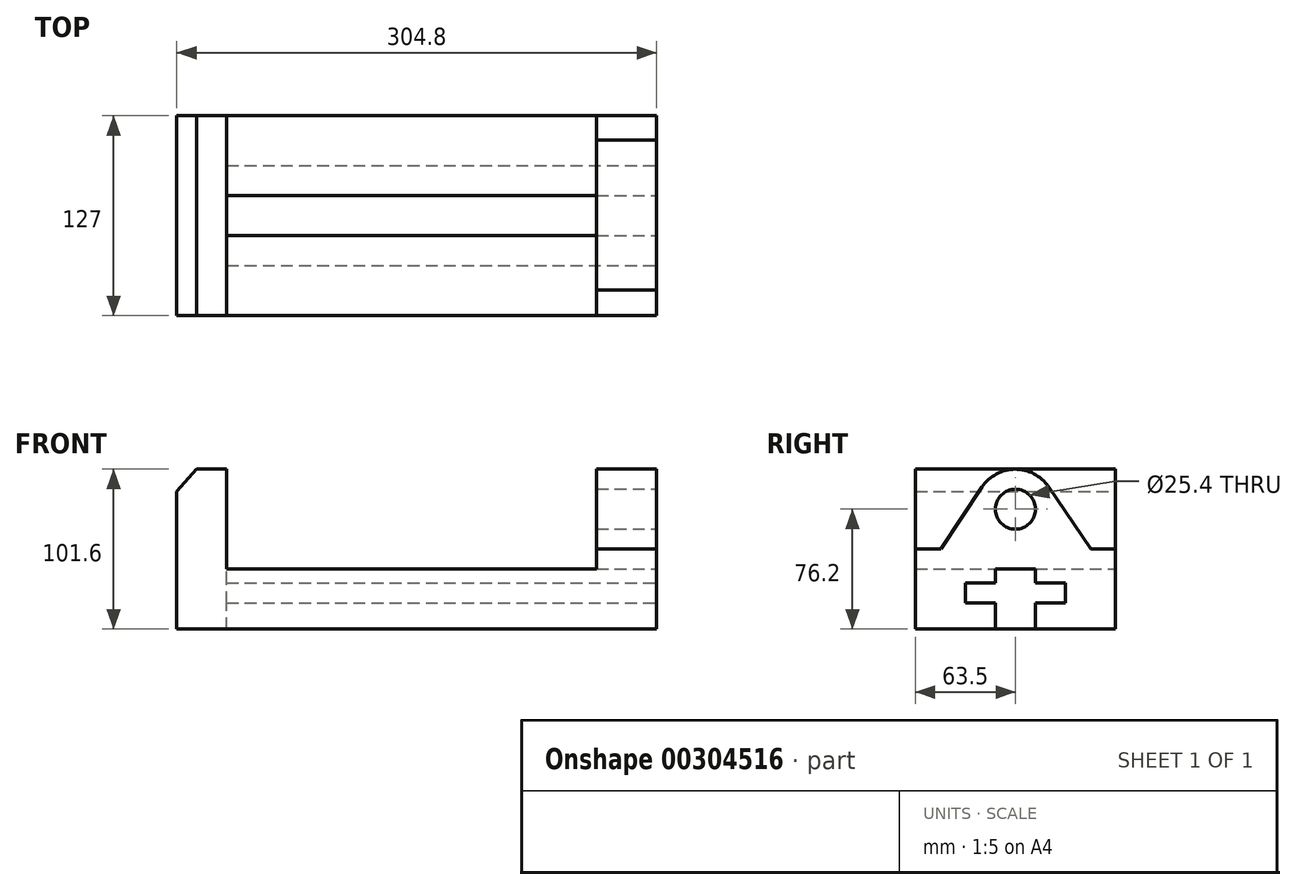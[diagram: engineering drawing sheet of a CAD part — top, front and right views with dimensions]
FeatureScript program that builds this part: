
annotation { "Feature Type Name" : "Feature", "Feature Type Description" : "" }
export const myFeature = defineFeature(function(context is Context, id is Id, definition is map)
    precondition{}
    {
        {
            var Q0;
            Q0=qCreatedBy(makeId("Front.planeOp"),FACE);
            var sketch = newSketch(context, id + "F0", { "sketchPlane" : qUnion([Q0])});
            skLineSegment(sketch, "E0", {"start": v(0, 0) * mm, "end": v(304.8, 0) * mm});
            skLineSegment(sketch, "E1", {"start": v(304.8, 0) * mm, "end": v(304.8, 101.6) * mm});
            skLineSegment(sketch, "E2", {"start": v(304.8, 101.6) * mm, "end": v(266.7, 101.6) * mm});
            skLineSegment(sketch, "E3", {"start": v(266.7, 101.6) * mm, "end": v(266.7, 38.1) * mm});
            skLineSegment(sketch, "E4", {"start": v(266.7, 38.1) * mm, "end": v(31.75, 38.1) * mm});
            skLineSegment(sketch, "E5", {"start": v(31.75, 38.1) * mm, "end": v(31.75, 101.6) * mm});
            skLineSegment(sketch, "E6", {"start": v(31.75, 101.6) * mm, "end": v(12.7, 101.6) * mm});
            skLineSegment(sketch, "E7", {"start": v(0, 87.4) * mm, "end": v(0, 0) * mm});
            skLineSegment(sketch, "E8", {"start": v(12.7, 101.6) * mm, "end": v(0, 87.4) * mm});
            skSolve(sketch);
        }
        {
            var Q0;
            Q0=makeQuery(id+"F0.imprint","IMPRINT",FACE,{"disambiguationData":[TD([[makeQuery(id+"F0.imprint","IMPRINT",EDGE,{"derivedFrom":sQuery(id+"F0.wireOp",EDGE,"E0")}),1.0]])]});
            extrude(context, id + "F1", {"entities" : qUnion([Q0]), "endBound" : BoundingType.SYMMETRIC, "depth" : 127 * mm});
        }
        {
            var Q0;
            Q0=makeQuery(id+"F1.opExtrude","SWEPT_FACE",FACE,{"disambiguationData":[OSD([sQuery(id+"F0.wireOp",EDGE,"E1")])]});
            var sketch = newSketch(context, id + "F2", { "sketchPlane" : qUnion([Q0])});
            skLineSegment(sketch, "E9", {"start": v(-63.5, 50.8) * mm, "end": v(-63.5, 0) * mm});
            skLineSegment(sketch, "E10", {"start": v(-63.5, 0) * mm, "end": v(63.5, 0) * mm});
            skLineSegment(sketch, "E11", {"start": v(63.5, 0) * mm, "end": v(63.5, 50.8) * mm});
            skLineSegment(sketch, "E12", {"start": v(63.5, 50.8) * mm, "end": v(48.09, 50.8) * mm});
            skLineSegment(sketch, "E13", {"start": v(-63.5, 50.8) * mm, "end": v(-47.16, 50.8) * mm});
            skLineSegment(sketch, "E14", {"start": v(-12.7, 38.1) * mm, "end": v(12.7, 38.1) * mm});
            skLineSegment(sketch, "E15", {"start": v(12.7, 38.1) * mm, "end": v(12.7, 29.21) * mm});
            skLineSegment(sketch, "E16", {"start": v(12.7, 29.21) * mm, "end": v(31.75, 29.21) * mm});
            skLineSegment(sketch, "E17", {"start": v(31.75, 29.21) * mm, "end": v(31.75, 16.51) * mm});
            skLineSegment(sketch, "E18", {"start": v(31.75, 16.51) * mm, "end": v(12.7, 16.51) * mm});
            skLineSegment(sketch, "E19", {"start": v(12.7, 16.51) * mm, "end": v(12.7, 0) * mm});
            skLineSegment(sketch, "E20", {"start": v(12.7, 0) * mm, "end": v(-12.7, 0) * mm});
            skLineSegment(sketch, "E21", {"start": v(-12.7, 0) * mm, "end": v(-12.7, 16.51) * mm});
            skLineSegment(sketch, "E22", {"start": v(-12.7, 16.51) * mm, "end": v(-31.75, 16.51) * mm});
            skLineSegment(sketch, "E23", {"start": v(-31.75, 16.51) * mm, "end": v(-31.75, 29.21) * mm});
            skLineSegment(sketch, "E24", {"start": v(-31.75, 29.21) * mm, "end": v(-12.7, 29.21) * mm});
            skLineSegment(sketch, "E25", {"start": v(-12.7, 29.21) * mm, "end": v(-12.7, 38.1) * mm});
            skLineSegment(sketch, "E26", {"start": v(0, 0) * mm, "end": v(0, 101.6) * mm, "construction": true});
            skArc(sketch, "E27", {"start": v(20.98, 90.52) * mm, "mid": v(-0.2, 101.6) * mm, "end": v(-21.2, 90.18) * mm});
            skLineSegment(sketch, "E28", {"start": v(-47.16, 50.8) * mm, "end": v(-21.2, 90.18) * mm});
            skLineSegment(sketch, "E29", {"start": v(20.98, 90.52) * mm, "end": v(48.09, 50.8) * mm});
            skCircle(sketch, "E30", {"center": v(0, 76.2) * mm, "radius": 12.7 * mm});
            skSolve(sketch);
        }
        {
            var Q0;
            {var subQ4=sQuery(id+"F2.wireOp",EDGE,"E13");Q0=makeQuery(id+"F2.imprint","IMPRINT",FACE,{"disambiguationData":[TD([[makeQuery(id+"F2.imprint","IMPRINT",EDGE,{"derivedFrom":subQ4}),1.0]])]});}
            var Q1;
            {var subQ5=sQuery(id+"F2.wireOp",EDGE,"E12");Q1=makeQuery(id+"F2.imprint","IMPRINT",FACE,{"disambiguationData":[TD([[makeQuery(id+"F2.imprint","IMPRINT",EDGE,{"derivedFrom":subQ5}),-1.0]])]});}
            extrude(context, id + "F3", {"entities" : qUnion([Q0, Q1]), "operationType" : NewBodyOperationType.REMOVE, "oppositeDirection" : true, "depth" : 38.1 * mm});
        }
        {
            var Q0;
            Q0=makeQuery(id+"F2.imprint","IMPRINT",FACE,{"disambiguationData":[TD([[makeQuery(id+"F2.imprint","IMPRINT",EDGE,{"derivedFrom":sQuery(id+"F2.wireOp",EDGE,"E30")}),1.0]])]});
            extrude(context, id + "F4", {"entities" : qUnion([Q0]), "operationType" : NewBodyOperationType.REMOVE, "oppositeDirection" : true, "depth" : 38.1 * mm});
        }
        {
            var Q0;
            Q0=makeQuery(id+"F2.imprint","IMPRINT",FACE,{"disambiguationData":[TD([[makeQuery(id+"F2.imprint","IMPRINT",EDGE,{"derivedFrom":sQuery(id+"F2.wireOp",EDGE,"E14")}),-1.0]])]});
            extrude(context, id + "F5", {"entities" : qUnion([Q0]), "operationType" : NewBodyOperationType.REMOVE, "oppositeDirection" : true, "depth" : 273.05 * mm});
        }
    });
